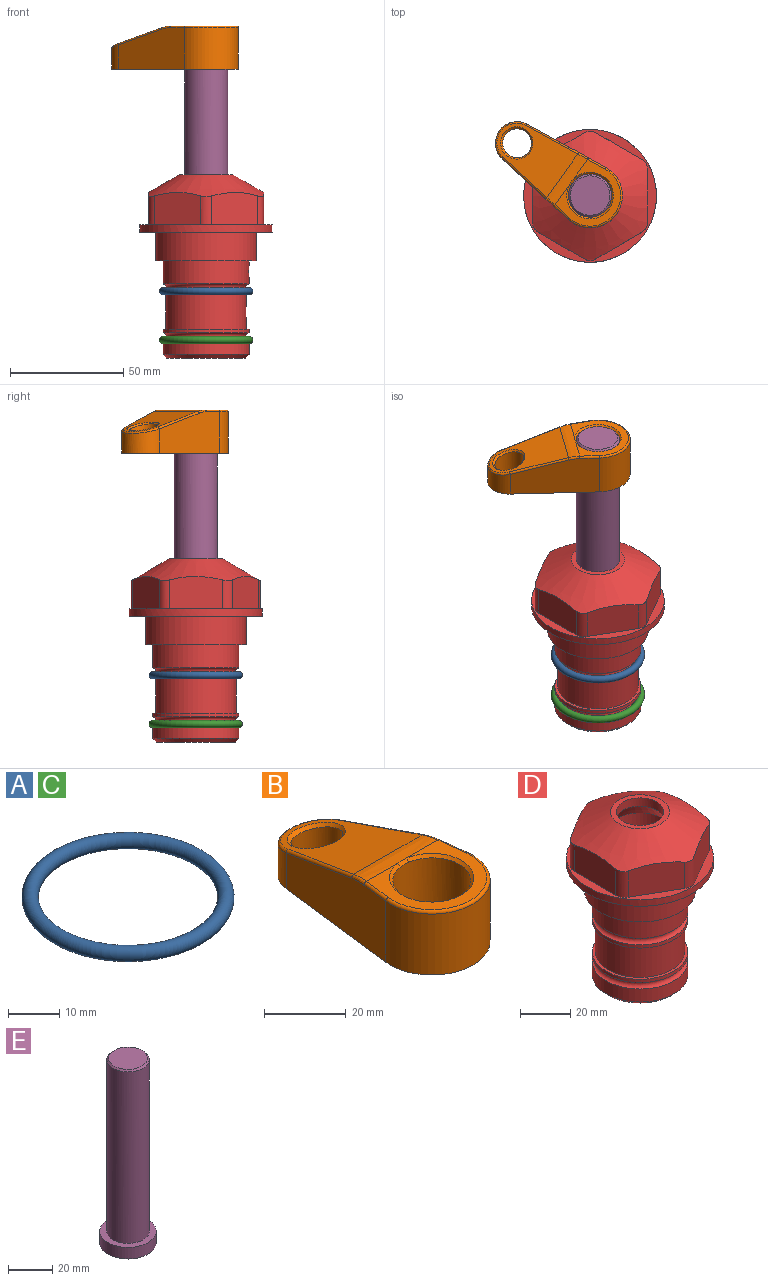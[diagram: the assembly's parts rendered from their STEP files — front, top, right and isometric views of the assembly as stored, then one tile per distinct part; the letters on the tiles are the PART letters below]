
ASSEMBLY  parts=5 mates=4
PART A: 1 faces, bbox 44.7x44.7x3.2 mm
  f0: torus R=19.05mm, axis (0,0,1), area 1193.9mm2
PART B: 31 faces, bbox 31.7x65.5x19.8 mm
  f0: plane 39.12x18.26mm, normal (0.99,0.12,0), area 612.2mm2, adj f1,f4,f7,f11,f13,f15
  f1: cylinder r=9.53mm len=18.91mm, axis (0,0,-1), area 296.1mm2, adj f0,f2,f7,f17
  f2: plane 39.12x18.26mm, normal (-0.99,0.12,0), area 612.2mm2, adj f1,f4,f7,f12,f14,f16
  f3: cylinder r=6.35mm len=12.7mm, axis (0,0,-1), area 362.4mm2, adj f7,f18
  f4: cylinder r=14.29mm len=28.58mm, axis (0,0,-1), area 882.2mm2, adj f0,f2,f7,f10
  f5: cylinder r=9.53mm len=19.05mm, axis (0,0,-1), area 1092.6mm2, adj f7,f19,f20
  f6: plane 26.99x23.69mm, normal (0,0,1), area 216.2mm2, adj f9,f10,f11,f12,f19
  f7: plane 63.5x28.58mm, normal (0,0,-1), area 661.8mm2, adj f0,f1,f2,f3,f4,f5,f22,f23
  f8: plane 33.52x23.6mm, normal (0,0.26,0.97), area 486mm2, adj f9,f15,f16,f17,f18
  f9: cylinder r=19.05mm len=24.72mm, axis (1,0,0), area 120.4mm2, adj f6,f8,f13,f14,f20
  f10: torus R=13.49mm, axis (0,0,1), area 59mm2, adj f4,f6,f11,f12
  f11: cylinder r=0.79mm len=8.67mm, axis (0.12,-0.99,0), area 10.8mm2, adj f0,f6,f10,f13
  f12: cylinder r=0.79mm len=8.67mm, axis (0.12,0.99,0), area 10.8mm2, adj f2,f6,f10,f14
  f13: bspline ~4.95x1.42mm, area 6.1mm2, adj f0,f9,f11,f15
  f14: bspline ~4.95x1.42mm, area 6.1mm2, adj f2,f9,f12,f16
  f15: cylinder r=0.79mm len=25.95mm, axis (0.12,-0.96,0.26), area 32.9mm2, adj f0,f8,f13,f17
  f16: cylinder r=0.79mm len=25.95mm, axis (0.12,0.96,-0.26), area 32.9mm2, adj f2,f8,f14,f17
  f17: bspline ~18.91x8.38mm, area 30mm2, adj f1,f8,f15,f16
  f18: bspline ~14.29x14.29mm, area 48.3mm2, adj f3,f8
  f19: cone r=9.53mm half-angle=45deg, axis (0,0,1), area 66.5mm2, adj f5,f6,f20
  f20: bspline ~3.22x0.96mm, area 3.5mm2, adj f5,f9,f19
  f21: plane 2.75x2.72mm, normal (0,0,-1), area 2.9mm2, adj f23,f25,f28
  f22: plane 23.05x15.88mm, normal (-0.99,-0.12,0), area 323.6mm2, adj f7,f25,f26,f27,f28,f29
  f23: plane 23.05x15.88mm, normal (0.99,-0.12,0), area 323.6mm2, adj f7,f21,f25,f27,f28,f30
  f24: cylinder r=9.53mm len=10.69mm, axis (0,0,-1), area 114.7mm2, adj f7,f27,f29,f30
  f25: cylinder r=12.7mm len=20.59mm, axis (0,0,-1), area 381.1mm2, adj f7,f21,f22,f23,f26,f28
  f26: plane 2.75x2.72mm, normal (0,0,-1), area 2.9mm2, adj f22,f25,f28
  f27: plane 19.72x18.37mm, normal (0,-0.26,-0.97), area 291.8mm2, adj f22,f23,f24,f28,f29,f30
  f28: cylinder r=15.88mm len=19.92mm, axis (1,0,0), area 54.8mm2, adj f21,f22,f23,f25,f26,f27
  f29: cylinder r=1.59mm len=11mm, axis (0,0,-1), area 34.7mm2, adj f7,f22,f24,f27
  f30: cylinder r=1.59mm len=11mm, axis (0,0,-1), area 34.7mm2, adj f7,f23,f24,f27
PART C: same geometry as A
PART D: 36 faces, bbox 58.7x58.7x81 mm
  f0: cylinder r=17.78mm len=35.56mm, axis (0,0,1), area 1670.8mm2, adj f23,f24,f31
  f1: cylinder r=19.05mm len=38.1mm, axis (0,0,1), area 1191.9mm2, adj f26,f27,f30
  f2: plane 58.66x58.66mm, normal (0,0,-1), area 1150.6mm2, adj f3,f28
  f3: cylinder r=29.33mm len=58.66mm, axis (0,0,-1), area 585.1mm2, adj f2,f4
  f4: plane 58.66x58.66mm, normal (0,0,1), area 475.9mm2, adj f3,f5,f6,f7,f8,f9,f10,f11
  f5: plane 20.32x14.34mm, normal (-0.5,0.87,0), area 324.4mm2, adj f4,f15,f16,f17
  f6: plane 20.32x14.34mm, normal (0.5,0.87,0), area 324.4mm2, adj f4,f14,f15,f17
  f7: plane 23.48x14.34mm, normal (1,0,0), area 324.4mm2, adj f4,f13,f14,f17
  f8: plane 20.32x14.34mm, normal (0.5,-0.87,0), area 324.4mm2, adj f4,f12,f13,f17
  f9: plane 20.32x14.34mm, normal (-0.5,-0.87,0), area 324.4mm2, adj f4,f11,f12,f17
  f10: plane 23.48x14.34mm, normal (-1,0,0), area 324.4mm2, adj f4,f11,f16,f17
  f11: cylinder r=5.08mm len=12.85mm, axis (0,0,-1), area 67.2mm2, adj f4,f9,f10,f17
  f12: cylinder r=5.08mm len=12.85mm, axis (0,0,-1), area 67.2mm2, adj f4,f8,f9,f17
  f13: cylinder r=5.08mm len=12.85mm, axis (0,0,-1), area 67.2mm2, adj f4,f7,f8,f17
  f14: cylinder r=5.08mm len=12.85mm, axis (0,0,-1), area 67.2mm2, adj f4,f6,f7,f17
  f15: cylinder r=5.08mm len=12.85mm, axis (0,0,-1), area 67.2mm2, adj f4,f5,f6,f17
  f16: cylinder r=5.08mm len=12.85mm, axis (0,0,-1), area 67.2mm2, adj f4,f5,f10,f17
  f17: cone r=11.73mm half-angle=60deg, axis (0,0,-1), area 2071.8mm2, adj f5,f6,f7,f8,f9,f10,f11,f12
  f18: plane 23.46x23.46mm, normal (0,0,1), area 147.4mm2, adj f17,f35
  f19: plane 34.93x34.93mm, normal (0,0,-1), area 958mm2, adj f29
  f20: cylinder r=19.05mm len=38.1mm, axis (0,0,1), area 760.1mm2, adj f21,f29
  f21: torus R=19.05mm, axis (0,0,1), area 565.3mm2, adj f20,f22
  f22: cylinder r=19.05mm len=38.1mm, axis (0,0,1), area 190mm2, adj f21,f23
  f23: plane 38.1x38.1mm, normal (0,0,1), area 146.9mm2, adj f0,f22
  f24: plane 38.1x38.1mm, normal (0,0,-1), area 146.9mm2, adj f0,f25
  f25: cylinder r=19.05mm len=38.1mm, axis (0,0,1), area 190mm2, adj f24,f26
  f26: torus R=19.05mm, axis (0,0,1), area 565.3mm2, adj f1,f25
  f27: plane 44.45x44.45mm, normal (0,0,-1), area 411.7mm2, adj f1,f28
  f28: cylinder r=22.23mm len=44.45mm, axis (0,0,1), area 1773.5mm2, adj f2,f27
  f29: cone r=19.05mm half-angle=45deg, axis (0,0,1), area 257.5mm2, adj f19,f20
  f30: cylinder r=3.17mm len=6.75mm, axis (-1,0,0), area 128mm2, adj f1,f33
  f31: cylinder r=3.17mm len=6.35mm, axis (-1,0,0), area 102.5mm2, adj f0,f33
  f32: plane 25.4x25.4mm, normal (0,0,1), area 506.7mm2, adj f33
  f33: cylinder r=12.7mm len=66.42mm, axis (0,0,-1), area 5236.2mm2, adj f30,f31,f32,f34
  f34: cone r=9.53mm half-angle=30deg, axis (0,0,-1), area 443.4mm2, adj f33,f35
  f35: cylinder r=9.53mm len=19.05mm, axis (0,0,-1), area 240.9mm2, adj f18,f34
PART E: 6 faces, bbox 25.4x25.4x101.6 mm
  f0: plane 17.46x17.46mm, normal (0,0,1), area 239.5mm2, adj f5
  f1: plane 25.4x25.4mm, normal (0,0,-1), area 506.7mm2, adj f2
  f2: cylinder r=12.7mm len=25.4mm, axis (0,0,1), area 506.7mm2, adj f1,f3
  f3: plane 25.4x25.4mm, normal (0,0,1), area 221.7mm2, adj f2,f4
  f4: cylinder r=9.53mm len=94.46mm, axis (0,0,1), area 5653mm2, adj f3,f5
  f5: cone r=8.73mm half-angle=45deg, axis (0,0,-1), area 64.4mm2, adj f0,f4
PLACE A t=(0,0,-1.59)mm
PLACE B rot(axis=(0,0,1),54.3deg) t=(0,0,27.55)mm
PLACE C t=(0,0,-23.18)mm
PLACE D at identity fixed
PLACE E rot(axis=(0,0,1),54.3deg) t=(0,0,27.55)mm
MATE fastened A.f0 <-> D.f0  axis (0,0,1) through (0,0,-26.1)mm
MATE fastened C.f0 <-> D.f0  axis (0,0,1) through (0,0,-47.69)mm
MATE cylindrical E.f2 <-> D.f0  axis (0,0,-1) through (0,0,-10.55)mm
MATE fastened B.f4 <-> E.f2  axis (0,0,1) through (0,0,91.05)mm
